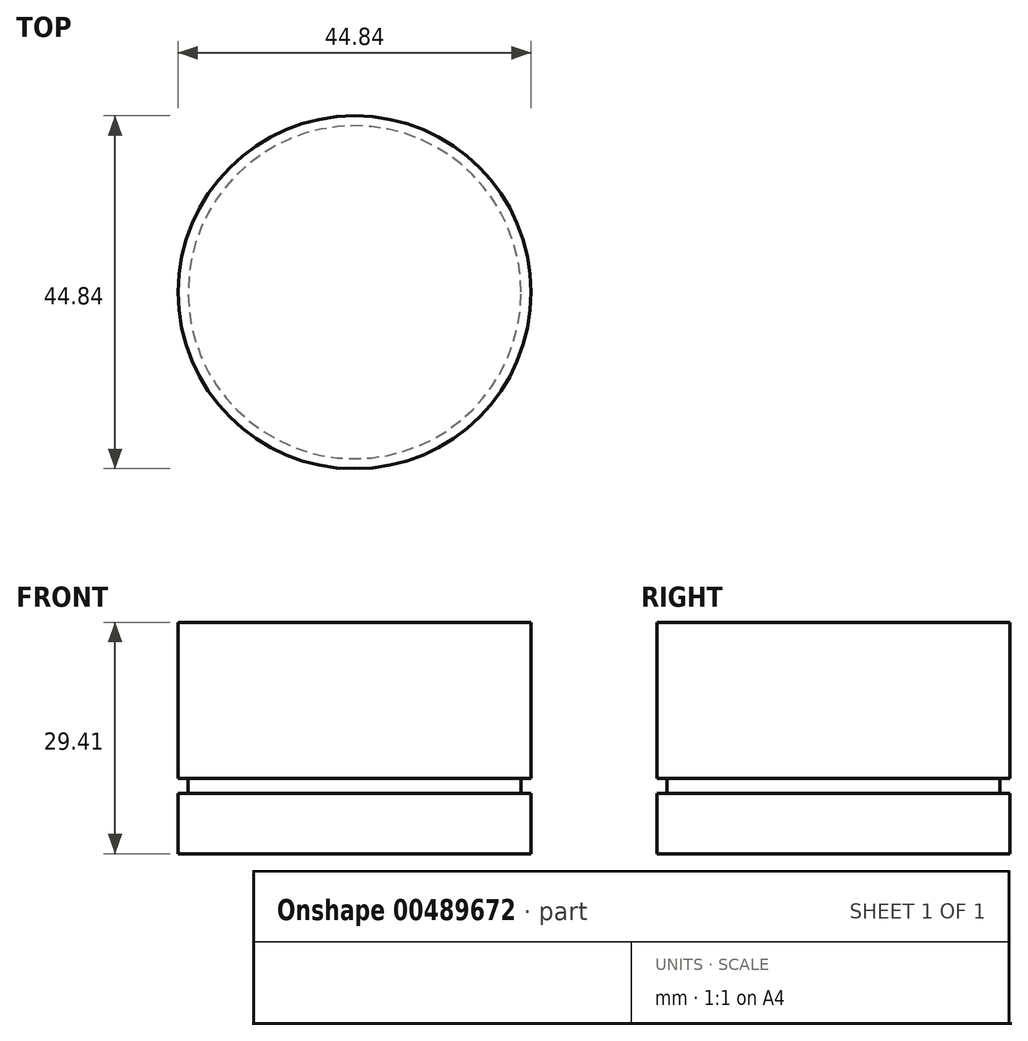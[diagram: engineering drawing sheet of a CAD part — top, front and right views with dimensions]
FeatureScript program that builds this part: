
annotation { "Feature Type Name" : "Feature", "Feature Type Description" : "" }
export const myFeature = defineFeature(function(context is Context, id is Id, definition is map)
    precondition{}
    {
        {
            var Q0;
            Q0=qCreatedBy(makeId("Front.planeOp"),FACE);
            var sketch = newSketch(context, id + "F0", { "sketchPlane" : qUnion([Q0])});
            skLineSegment(sketch, "E0", {"start": v(22.42, 29.41) * mm, "end": v(22.42, 9.57) * mm});
            skLineSegment(sketch, "E1", {"start": v(21.15, 9.57) * mm, "end": v(21.15, 7.64) * mm});
            skLineSegment(sketch, "E2", {"start": v(21.15, 7.64) * mm, "end": v(22.42, 7.64) * mm});
            skLineSegment(sketch, "E3", {"start": v(22.42, 7.64) * mm, "end": v(22.42, 0) * mm});
            skLineSegment(sketch, "E4", {"start": v(22.42, 0) * mm, "end": v(0, 0) * mm});
            skLineSegment(sketch, "E5", {"start": v(0, 0) * mm, "end": v(0, 29.41) * mm});
            skLineSegment(sketch, "E6", {"start": v(0, 29.41) * mm, "end": v(22.42, 29.41) * mm});
            skLineSegment(sketch, "E7", {"start": v(21.15, 9.57) * mm, "end": v(22.42, 9.57) * mm});
            skSolve(sketch);
        }
        {
            var Q0;
            Q0=makeQuery(id+"F0.imprint","IMPRINT",FACE,{"disambiguationData":[TD([[makeQuery(id+"F0.imprint","IMPRINT",EDGE,{"derivedFrom":sQuery(id+"F0.wireOp",EDGE,"E0")}),-1.0]])]});
            var Q1;
            Q1=sQuery(id+"F0.wireOp",EDGE,"E5");
            revolve(context, id + "F1", {"entities" : qUnion([Q0]), "axis" : qUnion([Q1]), "revolveType" : RevolveType.FULL});
        }
    });
